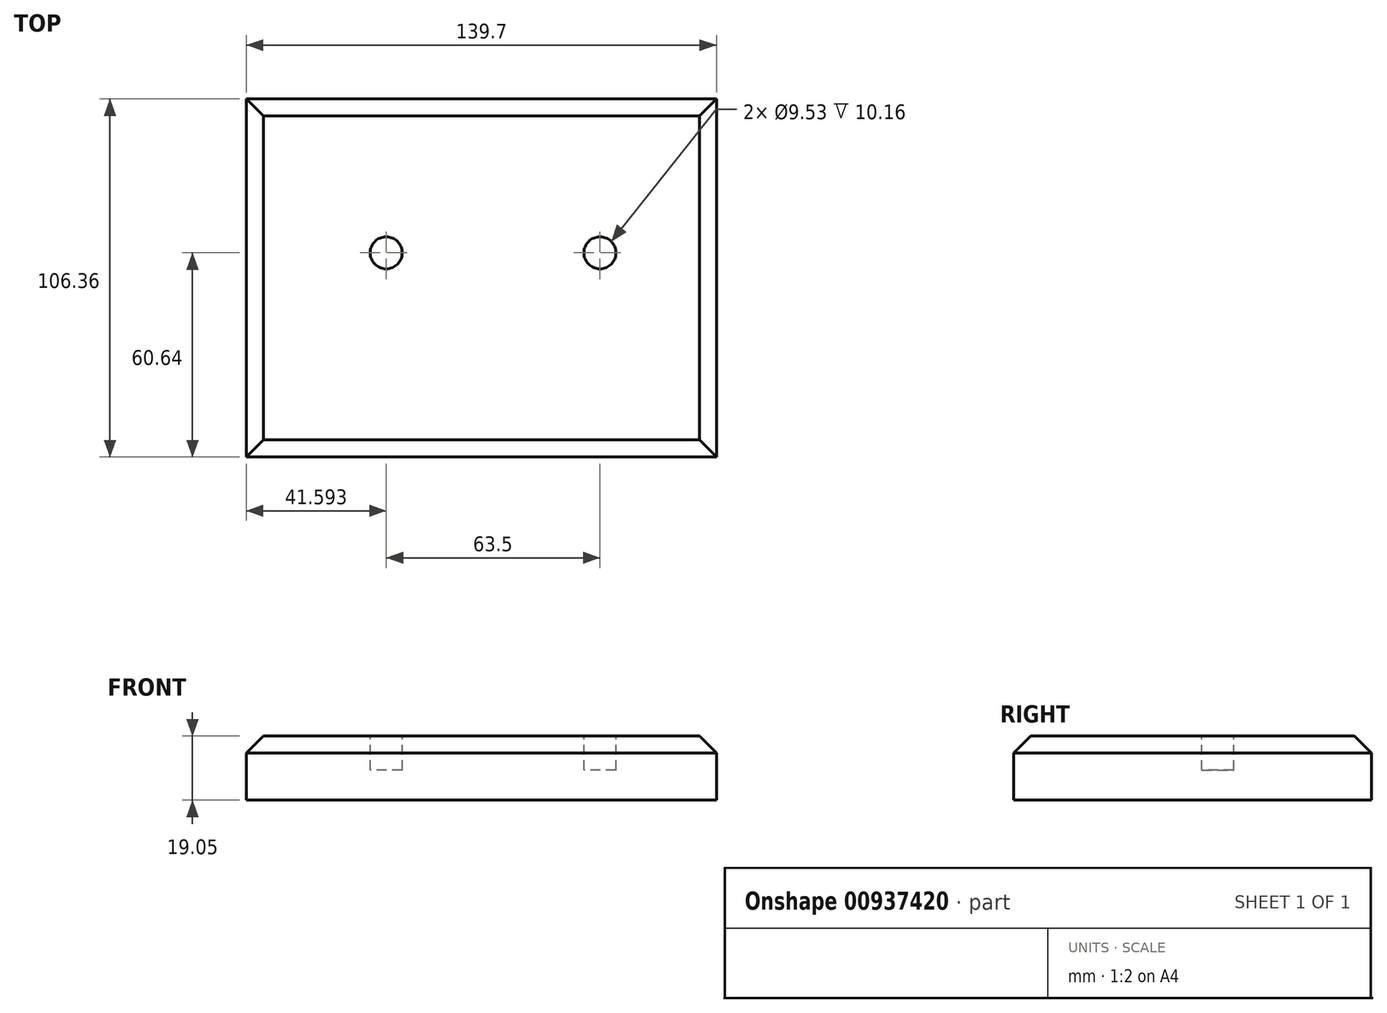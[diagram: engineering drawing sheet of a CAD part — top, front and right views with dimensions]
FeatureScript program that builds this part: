
annotation { "Feature Type Name" : "Feature", "Feature Type Description" : "" }
export const myFeature = defineFeature(function(context is Context, id is Id, definition is map)
    precondition{}
    {
        {
            var Q0;
            Q0=qCreatedBy(makeId("Top.planeOp"),FACE);
            var sketch = newSketch(context, id + "F0", { "sketchPlane" : qUnion([Q0])});
            skLineSegment(sketch, "E0.bottom", {"start": v(0, 0) * mm, "end": v(139.7, 0) * mm});
            skLineSegment(sketch, "E0.top", {"start": v(0, -106.36) * mm, "end": v(139.7, -106.36) * mm});
            skLineSegment(sketch, "E0.left", {"start": v(0, 0) * mm, "end": v(0, -106.36) * mm});
            skLineSegment(sketch, "E0.right", {"start": v(139.7, 0) * mm, "end": v(139.7, -106.36) * mm});
            skSolve(sketch);
        }
        {
            var Q0;
            Q0=makeQuery(id+"F0.imprint","IMPRINT",FACE,{"disambiguationData":[TD([[makeQuery(id+"F0.imprint","IMPRINT",EDGE,{"derivedFrom":sQuery(id+"F0.wireOp",EDGE,"E0.bottom")}),-1.0]])]});
            extrude(context, id + "F1", {"entities" : qUnion([Q0]), "depth" : 19.05 * mm, "offsetDistance" : 25.4 * mm});
        }
        {
            var Q0;
            Q0=makeQuery(id+"F1.opExtrude","CAP_FACE",FACE,{"disambiguationData":[OSD([sQuery(id+"F0.wireOp",EDGE,"E0.bottom"),sQuery(id+"F0.wireOp",EDGE,"E0.top"),sQuery(id+"F0.wireOp",EDGE,"E0.left"),sQuery(id+"F0.wireOp",EDGE,"E0.right")])],"isStart":false});
            chamfer(context, id + "F2", {"entities" : qUnion([Q0]), "width" : 5.08 * mm, "tangentPropagation" : true});
        }
        {
            var Q0;
            Q0=makeQuery(id+"F1.opExtrude","CAP_FACE",FACE,{"disambiguationData":[OSD([sQuery(id+"F0.wireOp",EDGE,"E0.bottom"),sQuery(id+"F0.wireOp",EDGE,"E0.top"),sQuery(id+"F0.wireOp",EDGE,"E0.left"),sQuery(id+"F0.wireOp",EDGE,"E0.right")])],"isStart":false});
            var sketch = newSketch(context, id + "F3", { "sketchPlane" : qUnion([Q0])});
            skCircle(sketch, "E1", {"center": v(41.6, -45.72) * mm, "radius": 4.76 * mm});
            skCircle(sketch, "E2", {"center": v(105.1, -45.72) * mm, "radius": 4.76 * mm});
            skSolve(sketch);
        }
        {
            var Q0;
            Q0=makeQuery(id+"F3.imprint","IMPRINT",FACE,{"disambiguationData":[TD([[makeQuery(id+"F3.imprint","IMPRINT",EDGE,{"derivedFrom":sQuery(id+"F3.wireOp",EDGE,"E1")}),1.0]])]});
            var Q1;
            Q1=makeQuery(id+"F3.imprint","IMPRINT",FACE,{"disambiguationData":[TD([[makeQuery(id+"F3.imprint","IMPRINT",EDGE,{"derivedFrom":sQuery(id+"F3.wireOp",EDGE,"E2")}),1.0]])]});
            extrude(context, id + "F4", {"entities" : qUnion([Q0, Q1]), "operationType" : NewBodyOperationType.REMOVE, "oppositeDirection" : true, "depth" : 10.16 * mm, "offsetDistance" : 25.4 * mm});
        }
    });
